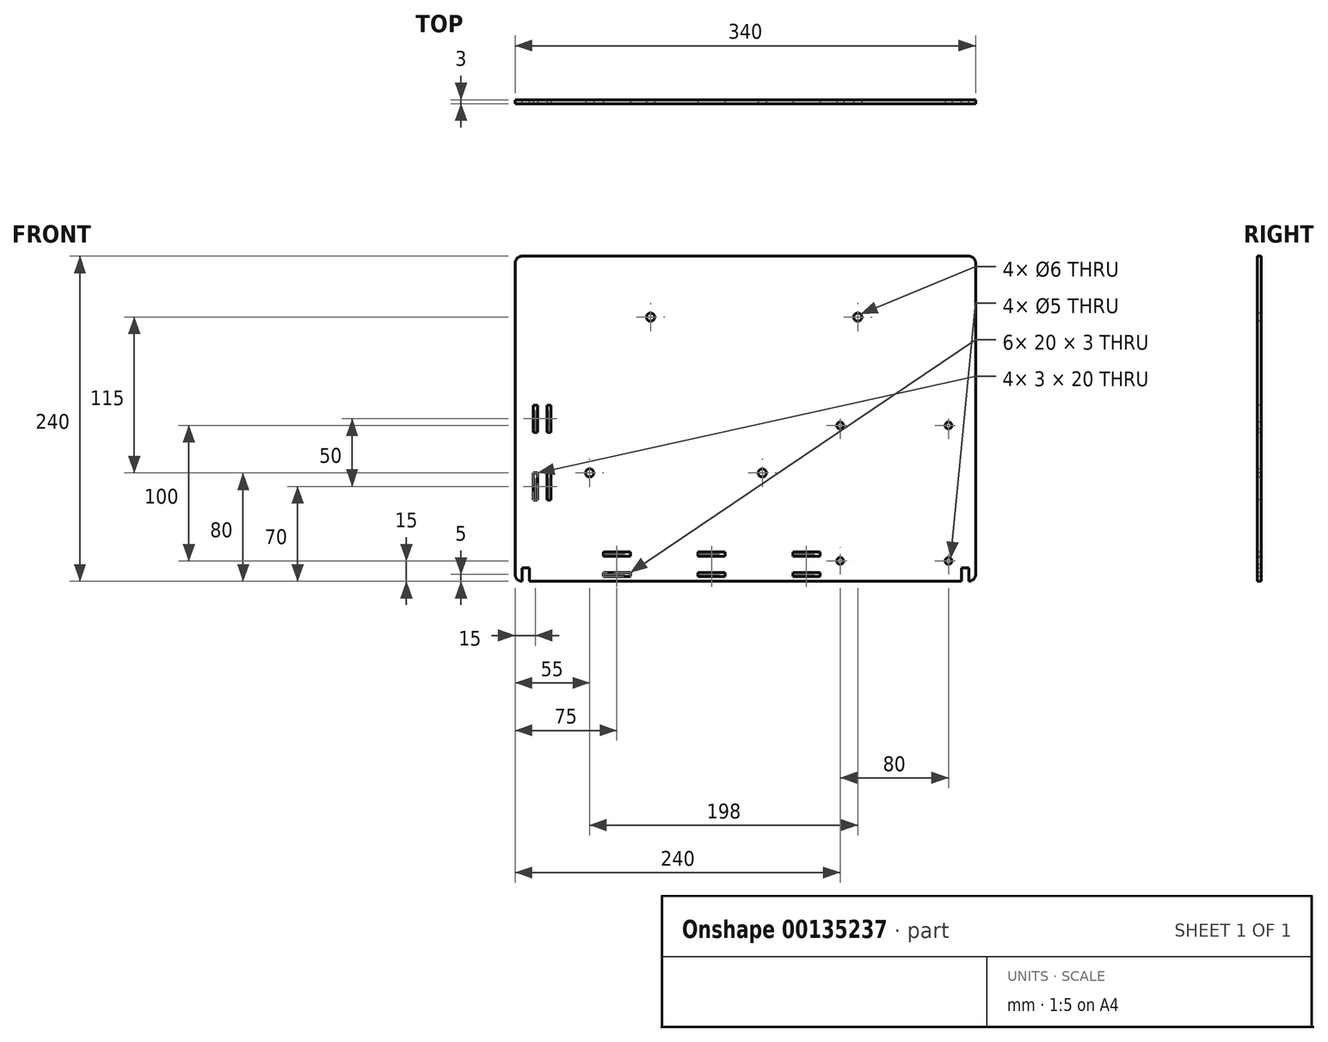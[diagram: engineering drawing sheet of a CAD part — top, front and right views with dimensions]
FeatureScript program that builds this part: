
annotation { "Feature Type Name" : "Feature", "Feature Type Description" : "" }
export const myFeature = defineFeature(function(context is Context, id is Id, definition is map)
    precondition{}
    {
        {
            var Q0;
            Q0=qCreatedBy(makeId("Front.planeOp"),FACE);
            var sketch = newSketch(context, id + "F0", { "sketchPlane" : qUnion([Q0])});
            skLineSegment(sketch, "E0.bottom", {"start": v(170, -120) * mm, "end": v(165, -120) * mm});
            skLineSegment(sketch, "E0.top", {"start": v(170, 120) * mm, "end": v(-170, 120) * mm});
            skLineSegment(sketch, "E0.left", {"start": v(170, -120) * mm, "end": v(170, 120) * mm});
            skLineSegment(sketch, "E0.right", {"start": v(-170, -120) * mm, "end": v(-170, 120) * mm});
            skPoint(sketch, "E0.middle", {"position": v(0, 0) * mm});
            skLineSegment(sketch, "E1", {"start": v(-165, -120) * mm, "end": v(-165, -110) * mm});
            skLineSegment(sketch, "E2", {"start": v(-165, -110) * mm, "end": v(-159.5, -110) * mm});
            skLineSegment(sketch, "E3", {"start": v(-159.5, -110) * mm, "end": v(-159.5, -120) * mm});
            skLineSegment(sketch, "E4", {"start": v(165, -120) * mm, "end": v(165, -110) * mm});
            skLineSegment(sketch, "E5", {"start": v(165, -110) * mm, "end": v(159.5, -110) * mm});
            skLineSegment(sketch, "E6", {"start": v(159.5, -110) * mm, "end": v(159.5, -120) * mm});
            skLineSegment(sketch, "E7.trimOffspring", {"start": v(-165, -120) * mm, "end": v(-170, -120) * mm});
            skLineSegment(sketch, "E8.trimOffspring", {"start": v(159.5, -120) * mm, "end": v(-159.5, -120) * mm});
            skSolve(sketch);
        }
        {
            var Q0;
            Q0=makeQuery(id+"F0.imprint","IMPRINT",FACE,{"disambiguationData":[TD([[makeQuery(id+"F0.imprint","IMPRINT",EDGE,{"derivedFrom":sQuery(id+"F0.wireOp",EDGE,"E0.bottom")}),-1.0]])]});
            extrude(context, id + "F1", {"entities" : qUnion([Q0]), "depth" : 3 * mm});
        }
        {
            var Q0;
            {var subQ0=sQuery(id+"F0.wireOp",EDGE,"E0.left");var subQ1=sQuery(id+"F0.wireOp",EDGE,"E0.bottom");var subQ2=sQuery(id+"F0.wireOp",EDGE,"E0.right");var subQ3=sQuery(id+"F0.wireOp",EDGE,"E0.top");Q0=makeQuery(id+"Fkeax6t5Ps2Em87_1.boolean.opBoolean","SPLIT",FACE,{"disambiguationData":[TD([makeQuery(id+"F1.opExtrude","SWEPT_FACE",FACE,{"disambiguationData":[OSD([subQ1])]})])],"derivedFrom":makeQuery(id+"F1.opExtrude","CAP_FACE",FACE,{"disambiguationData":[OSD([subQ1,subQ3,subQ0,subQ2])],"isStart":false})});}
            var sketch = newSketch(context, id + "F2", { "sketchPlane" : qUnion([Q0])});
            skCircle(sketch, "E9", {"center": v(-70, 75) * mm, "radius": 3 * mm});
            skCircle(sketch, "E10", {"center": v(83, 75) * mm, "radius": 3 * mm});
            skCircle(sketch, "E11", {"center": v(12.5, -40) * mm, "radius": 3 * mm});
            skCircle(sketch, "E12", {"center": v(-115, -40) * mm, "radius": 3 * mm});
            skSolve(sketch);
        }
        {
            var Q0;
            Q0=qSketchRegion(id+"F2",true);
            extrude(context, id + "F3", {"entities" : qUnion([Q0]), "operationType" : NewBodyOperationType.REMOVE, "endBound" : BoundingType.UP_TO_NEXT, "oppositeDirection" : true, "depth" : 25 * mm});
        }
        {
            var Q0;
            {var subQ0=sQuery(id+"F0.wireOp",EDGE,"E8.trimOffspring");var subQ1=sQuery(id+"F0.wireOp",EDGE,"E3");var subQ2=sQuery(id+"F0.wireOp",EDGE,"E4");var subQ3=sQuery(id+"F0.wireOp",EDGE,"E0.left");var subQ4=sQuery(id+"F0.wireOp",EDGE,"E0.bottom");var subQ5=sQuery(id+"F0.wireOp",EDGE,"E0.top");var subQ6=sQuery(id+"F0.wireOp",EDGE,"E7.trimOffspring");var subQ7=sQuery(id+"F0.wireOp",EDGE,"E0.right");var subQ8=sQuery(id+"F0.wireOp",EDGE,"E2");var subQ9=sQuery(id+"F0.wireOp",EDGE,"E1");var subQ10=sQuery(id+"F0.wireOp",EDGE,"E5");var subQ11=sQuery(id+"F0.wireOp",EDGE,"E6");Q0=makeQuery(id+"Fkeax6t5Ps2Em87_1.boolean.opBoolean","SPLIT",FACE,{"disambiguationData":[TD([makeQuery(id+"F1.opExtrude","SWEPT_FACE",FACE,{"disambiguationData":[OSD([subQ4])]})])],"derivedFrom":makeQuery(id+"F1.opExtrude","CAP_FACE",FACE,{"disambiguationData":[OSD([subQ4,subQ5,subQ3,subQ7,subQ9,subQ8,subQ1,subQ2,subQ10,subQ11,subQ6,subQ0])],"isStart":false})});}
            var sketch = newSketch(context, id + "F4", { "sketchPlane" : qUnion([Q0])});
            skCircle(sketch, "E13", {"center": v(70, -5) * mm, "radius": 2.5 * mm});
            skCircle(sketch, "E14", {"center": v(150, -5) * mm, "radius": 2.5 * mm});
            skCircle(sketch, "E15", {"center": v(150, -105) * mm, "radius": 2.5 * mm});
            skCircle(sketch, "E16", {"center": v(70, -105) * mm, "radius": 2.5 * mm});
            skSolve(sketch);
        }
        {
            var Q0;
            Q0 = qSketchRegion(id + "F4", true);
            extrude(context, id + "F5", {"entities" : qUnion([Q0]), "operationType" : NewBodyOperationType.REMOVE, "endBound" : BoundingType.UP_TO_NEXT, "oppositeDirection" : true, "depth" : 25 * mm});
        }
        {
            var Q0;
            Q0=makeQuery(id+"F1.opExtrude","CAP_FACE",FACE,{"disambiguationData":[OSD([sQuery(id+"F0.wireOp",EDGE,"E0.bottom"),sQuery(id+"F0.wireOp",EDGE,"E0.top"),sQuery(id+"F0.wireOp",EDGE,"E0.left"),sQuery(id+"F0.wireOp",EDGE,"E0.right"),sQuery(id+"F0.wireOp",EDGE,"E1"),sQuery(id+"F0.wireOp",EDGE,"E2"),sQuery(id+"F0.wireOp",EDGE,"E3"),sQuery(id+"F0.wireOp",EDGE,"E4"),sQuery(id+"F0.wireOp",EDGE,"E5"),sQuery(id+"F0.wireOp",EDGE,"E6"),sQuery(id+"F0.wireOp",EDGE,"E7.trimOffspring"),sQuery(id+"F0.wireOp",EDGE,"E8.trimOffspring")])],"isStart":false});
            var sketch = newSketch(context, id + "F6", { "sketchPlane" : qUnion([Q0])});
            skLineSegment(sketch, "E17.bottom", {"start": v(-85, -101.5) * mm, "end": v(-105, -101.5) * mm});
            skLineSegment(sketch, "E17.top", {"start": v(-85, -98.5) * mm, "end": v(-105, -98.5) * mm});
            skLineSegment(sketch, "E17.left", {"start": v(-85, -101.5) * mm, "end": v(-85, -98.5) * mm});
            skLineSegment(sketch, "E17.right", {"start": v(-105, -101.5) * mm, "end": v(-105, -98.5) * mm});
            skPoint(sketch, "E17.middle", {"position": v(-95, -100) * mm});
            skLineSegment(sketch, "E18.bottom", {"start": v(-15, -101.5) * mm, "end": v(-35, -101.5) * mm});
            skLineSegment(sketch, "E18.top", {"start": v(-15, -98.5) * mm, "end": v(-35, -98.5) * mm});
            skLineSegment(sketch, "E18.left", {"start": v(-15, -101.5) * mm, "end": v(-15, -98.5) * mm});
            skLineSegment(sketch, "E18.right", {"start": v(-35, -101.5) * mm, "end": v(-35, -98.5) * mm});
            skPoint(sketch, "E18.middle", {"position": v(-25, -100) * mm});
            skLineSegment(sketch, "E19.bottom", {"start": v(55, -101.5) * mm, "end": v(35, -101.5) * mm});
            skLineSegment(sketch, "E19.top", {"start": v(55, -98.5) * mm, "end": v(35, -98.5) * mm});
            skLineSegment(sketch, "E19.left", {"start": v(55, -101.5) * mm, "end": v(55, -98.5) * mm});
            skLineSegment(sketch, "E19.right", {"start": v(35, -101.5) * mm, "end": v(35, -98.5) * mm});
            skPoint(sketch, "E19.middle", {"position": v(45, -100) * mm});
            skLineSegment(sketch, "E20.bottom", {"start": v(-85, -116.5) * mm, "end": v(-105, -116.5) * mm});
            skLineSegment(sketch, "E20.top", {"start": v(-85, -113.5) * mm, "end": v(-105, -113.5) * mm});
            skLineSegment(sketch, "E20.left", {"start": v(-85, -116.5) * mm, "end": v(-85, -113.5) * mm});
            skLineSegment(sketch, "E20.right", {"start": v(-105, -116.5) * mm, "end": v(-105, -113.5) * mm});
            skPoint(sketch, "E20.middle", {"position": v(-95, -115) * mm});
            skPoint(sketch, "E20.middle.positionSnap0", {"position": v(-95, -101.5) * mm});
            skPoint(sketch, "E20.centerSnap0", {"position": v(-95, -101.5) * mm});
            skLineSegment(sketch, "E21.bottom", {"start": v(-15, -116.5) * mm, "end": v(-35, -116.5) * mm});
            skLineSegment(sketch, "E21.top", {"start": v(-15, -113.5) * mm, "end": v(-35, -113.5) * mm});
            skLineSegment(sketch, "E21.left", {"start": v(-15, -116.5) * mm, "end": v(-15, -113.5) * mm});
            skLineSegment(sketch, "E21.right", {"start": v(-35, -116.5) * mm, "end": v(-35, -113.5) * mm});
            skPoint(sketch, "E21.middle", {"position": v(-25, -115) * mm});
            skLineSegment(sketch, "E22.bottom", {"start": v(55, -116.5) * mm, "end": v(35, -116.5) * mm});
            skLineSegment(sketch, "E22.top", {"start": v(55, -113.5) * mm, "end": v(35, -113.5) * mm});
            skLineSegment(sketch, "E22.left", {"start": v(55, -116.5) * mm, "end": v(55, -113.5) * mm});
            skLineSegment(sketch, "E22.right", {"start": v(35, -116.5) * mm, "end": v(35, -113.5) * mm});
            skPoint(sketch, "E22.middle", {"position": v(45, -115) * mm});
            skLineSegment(sketch, "E23.bottom", {"start": v(-153.5, -10) * mm, "end": v(-156.5, -10) * mm});
            skLineSegment(sketch, "E23.top", {"start": v(-153.5, 10) * mm, "end": v(-156.5, 10) * mm});
            skLineSegment(sketch, "E23.left", {"start": v(-153.5, -10) * mm, "end": v(-153.5, 10) * mm});
            skLineSegment(sketch, "E23.right", {"start": v(-156.5, -10) * mm, "end": v(-156.5, 10) * mm});
            skPoint(sketch, "E23.middle", {"position": v(-155, 0) * mm});
            skLineSegment(sketch, "E24.bottom", {"start": v(-143.5, -10) * mm, "end": v(-146.5, -10) * mm});
            skLineSegment(sketch, "E24.top", {"start": v(-143.5, 10) * mm, "end": v(-146.5, 10) * mm});
            skLineSegment(sketch, "E24.left", {"start": v(-143.5, -10) * mm, "end": v(-143.5, 10) * mm});
            skLineSegment(sketch, "E24.right", {"start": v(-146.5, -10) * mm, "end": v(-146.5, 10) * mm});
            skPoint(sketch, "E24.middle", {"position": v(-145, 0) * mm});
            skLineSegment(sketch, "E25.bottom", {"start": v(-153.5, -60) * mm, "end": v(-156.5, -60) * mm});
            skLineSegment(sketch, "E25.top", {"start": v(-153.5, -40) * mm, "end": v(-156.5, -40) * mm});
            skLineSegment(sketch, "E25.left", {"start": v(-153.5, -60) * mm, "end": v(-153.5, -40) * mm});
            skLineSegment(sketch, "E25.right", {"start": v(-156.5, -60) * mm, "end": v(-156.5, -40) * mm});
            skPoint(sketch, "E25.middle", {"position": v(-155, -50) * mm});
            skLineSegment(sketch, "E26.bottom", {"start": v(-143.5, -60) * mm, "end": v(-146.5, -60) * mm});
            skLineSegment(sketch, "E26.top", {"start": v(-143.5, -40) * mm, "end": v(-146.5, -40) * mm});
            skLineSegment(sketch, "E26.left", {"start": v(-143.5, -60) * mm, "end": v(-143.5, -40) * mm});
            skLineSegment(sketch, "E26.right", {"start": v(-146.5, -60) * mm, "end": v(-146.5, -40) * mm});
            skPoint(sketch, "E26.middle", {"position": v(-145, -50) * mm});
            skPoint(sketch, "E26.middle.positionSnap0", {"position": v(-145, -10) * mm});
            skPoint(sketch, "E26.centerSnap0", {"position": v(-145, -10) * mm});
            skSolve(sketch);
        }
        {
            var Q0;
            Q0 = qSketchRegion(id + "F6", true);
            extrude(context, id + "F7", {"entities" : qUnion([Q0]), "operationType" : NewBodyOperationType.REMOVE, "endBound" : BoundingType.UP_TO_NEXT, "oppositeDirection" : true, "depth" : 25 * mm});
        }
        {
            var Q0;
            Q0=makeQuery(id+"F1.opExtrude","SWEPT_EDGE",EDGE,{"disambiguationData":[OSD([sQuery(id+"F0.wireOp",EDGE,"E0.top"),sQuery(id+"F0.wireOp",EDGE,"E0.right")])]});
            var Q1;
            Q1=makeQuery(id+"F1.opExtrude","SWEPT_EDGE",EDGE,{"disambiguationData":[OSD([sQuery(id+"F0.wireOp",EDGE,"E0.top"),sQuery(id+"F0.wireOp",EDGE,"E0.left")])]});
            var Q2;
            Q2=makeQuery(id+"F1.opExtrude","SWEPT_EDGE",EDGE,{"disambiguationData":[OSD([sQuery(id+"F0.wireOp",EDGE,"E0.bottom"),sQuery(id+"F0.wireOp",EDGE,"E0.left")])]});
            var Q3;
            Q3=makeQuery(id+"F1.opExtrude","SWEPT_EDGE",EDGE,{"disambiguationData":[OSD([sQuery(id+"F0.wireOp",EDGE,"E0.right"),sQuery(id+"F0.wireOp",EDGE,"E7.trimOffspring")])]});
            fillet(context, id + "F8", {"entities" : qUnion([Q0, Q1, Q2, Q3]), "radius" : 5 * mm, "tangentPropagation" : true, "allowEdgeOverflow" : false});
        }
    });
